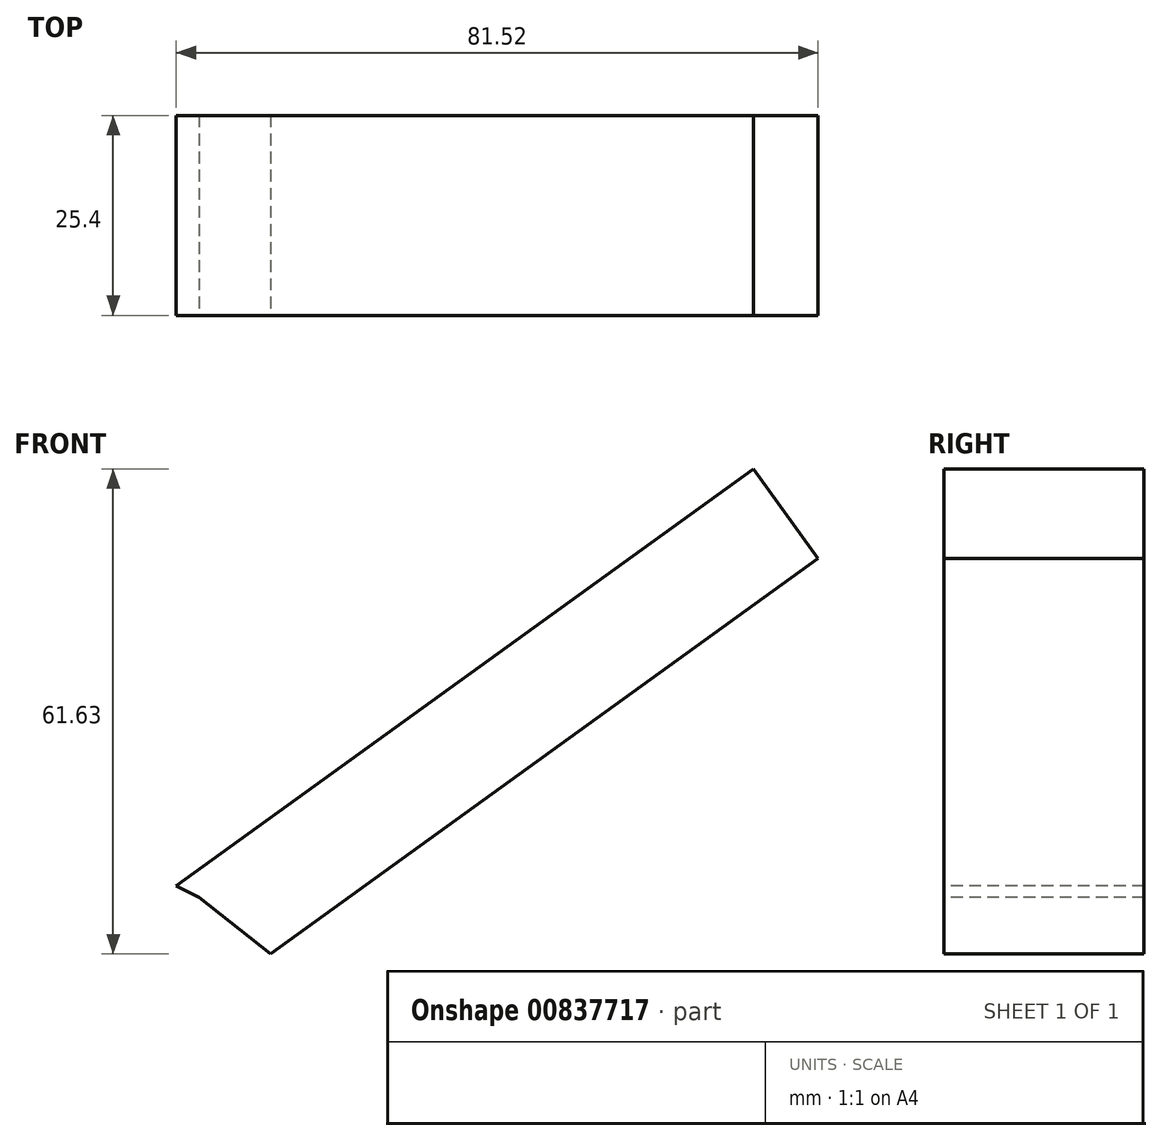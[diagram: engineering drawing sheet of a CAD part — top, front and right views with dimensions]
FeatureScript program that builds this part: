
annotation { "Feature Type Name" : "Feature", "Feature Type Description" : "" }
export const myFeature = defineFeature(function(context is Context, id is Id, definition is map)
    precondition{}
    {
        {
            var Q0;
            Q0=qCreatedBy(makeId("Front.planeOp"),FACE);
            var sketch = newSketch(context, id + "F0", { "sketchPlane" : qUnion([Q0])});
            skLineSegment(sketch, "E0", {"start": v(-51.4, -11.95) * mm, "end": v(21.9, 41.04) * mm});
            skLineSegment(sketch, "E1", {"start": v(21.9, 41.04) * mm, "end": v(30.11, 29.67) * mm});
            skLineSegment(sketch, "E2", {"start": v(30.11, 29.67) * mm, "end": v(-39.41, -20.6) * mm});
            skLineSegment(sketch, "E3", {"start": v(-39.41, -20.6) * mm, "end": v(-48.54, -13.42) * mm});
            skLineSegment(sketch, "E4", {"start": v(-48.54, -13.42) * mm, "end": v(-48.54, -13.42) * mm});
            skLineSegment(sketch, "E5", {"start": v(-51.4, -11.95) * mm, "end": v(-48.54, -13.42) * mm});
            skSolve(sketch);
        }
        {
            var Q0;
            Q0=sQuery(id+"F0.wireOp",EDGE,"E1");
            var Q1;
            Q1=sQuery(id+"F0.wireOp",EDGE,"E2");
            var Q2;
            Q2=sQuery(id+"F0.wireOp",EDGE,"E3");
            var Q3;
            Q3=sQuery(id+"F0.wireOp",EDGE,"E5");
            var Q4;
            Q4=sQuery(id+"F0.wireOp",EDGE,"E0");
            extrude(context, id + "F1", {"bodyType" : ToolBodyType.SURFACE, "surfaceEntities" : qUnion([Q0, Q1, Q2, Q3, Q4]), "depth" : 25.4 * mm, "offsetDistance" : 25.4 * mm});
        }
    });
